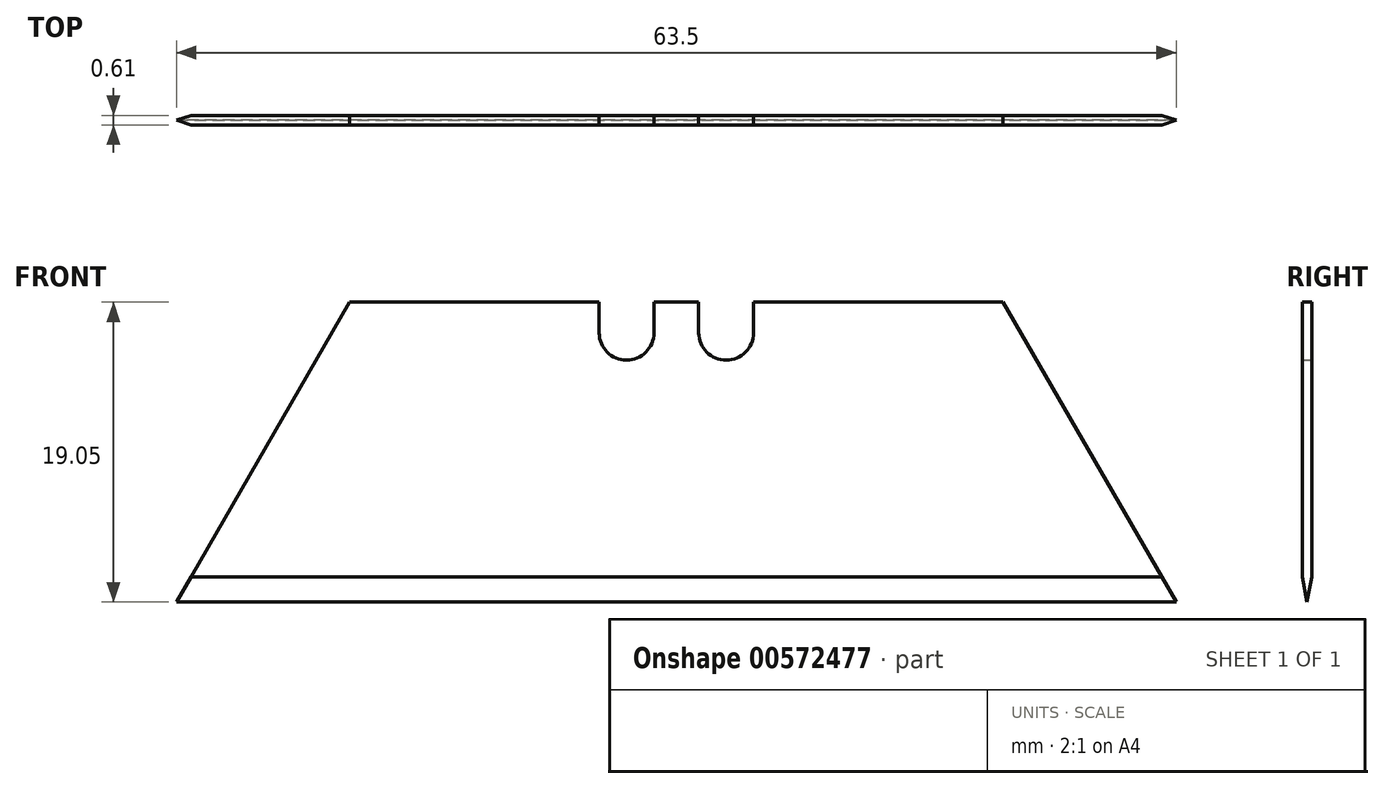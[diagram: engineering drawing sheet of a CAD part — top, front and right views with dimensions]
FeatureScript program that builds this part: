
annotation { "Feature Type Name" : "Feature", "Feature Type Description" : "" }
export const myFeature = defineFeature(function(context is Context, id is Id, definition is map)
    precondition{}
    {
        {
            var Q0;
            Q0=qCreatedBy(makeId("Front.planeOp"),FACE);
            var sketch = newSketch(context, id + "F0", { "sketchPlane" : qUnion([Q0])});
            skLineSegment(sketch, "E0", {"start": v(0, 0) * mm, "end": v(31.75, 0) * mm});
            skLineSegment(sketch, "E1", {"start": v(31.75, 0) * mm, "end": v(20.75, 19.05) * mm});
            skLineSegment(sketch, "E2", {"start": v(20.75, 19.05) * mm, "end": v(0, 19.05) * mm});
            skLineSegment(sketch, "E3", {"start": v(0, 19.05) * mm, "end": v(0, 0) * mm});
            skSolve(sketch);
        }
        {
            var Q0;
            Q0=makeQuery(id+"F0.imprint","IMPRINT",FACE,{"disambiguationData":[TD([[makeQuery(id+"F0.imprint","IMPRINT",EDGE,{"derivedFrom":sQuery(id+"F0.wireOp",EDGE,"E0")}),1.0]])]});
            extrude(context, id + "F1", {"entities" : qUnion([Q0]), "depth" : 0.6 * mm, "offsetDistance" : 25.4 * mm});
        }
        {
            var Q0;
            Q0=qCreatedBy(makeId("Front.planeOp"),FACE);
            var sketch = newSketch(context, id + "F2", { "sketchPlane" : qUnion([Q0])});
            skLineSegment(sketch, "E4.0.0", {"start": v(20.75, 19.05) * mm, "end": v(0, 19.05) * mm});
            skLineSegment(sketch, "E4.0.1", {"start": v(0, 19.05) * mm, "end": v(0, 0) * mm});
            skLineSegment(sketch, "E4.0.2", {"start": v(0, 0) * mm, "end": v(31.75, 0) * mm});
            skLineSegment(sketch, "E4.0.3", {"start": v(31.75, 0) * mm, "end": v(20.75, 19.05) * mm});
            skLineSegment(sketch, "E5.bottom", {"start": v(4.9, 17.1) * mm, "end": v(1.42, 17.1) * mm});
            skLineSegment(sketch, "E5.top", {"start": v(4.9, 21) * mm, "end": v(1.42, 21) * mm});
            skLineSegment(sketch, "E5.left", {"start": v(4.9, 17.1) * mm, "end": v(4.9, 21) * mm});
            skLineSegment(sketch, "E5.right", {"start": v(1.42, 17.1) * mm, "end": v(1.42, 21) * mm});
            skPoint(sketch, "E5.middle", {"position": v(3.16, 19.05) * mm});
            skArc(sketch, "E6", {"start": v(1.42, 17.1) * mm, "mid": v(3.16, 15.37) * mm, "end": v(4.9, 17.1) * mm});
            skSolve(sketch);
        }
        {
            var Q0;
            Q0=makeQuery(id+"F2.imprint","IMPRINT",FACE,{"disambiguationData":[TD([[makeQuery(id+"F2.imprint","IMPRINT",EDGE,{"derivedFrom":sQuery(id+"F2.wireOp",EDGE,"E5.bottom")}),1.0]])]});
            var Q1;
            {var subQ5=sQuery(id+"F2.wireOp",EDGE,"E5.bottom");Q1=makeQuery(id+"F2.imprint","IMPRINT",FACE,{"disambiguationData":[TD([[makeQuery(id+"F2.imprint","IMPRINT",EDGE,{"derivedFrom":subQ5}),-1.0]])]});}
            extrude(context, id + "F3", {"entities" : qUnion([Q0, Q1]), "operationType" : NewBodyOperationType.REMOVE, "depth" : 25.4 * mm, "offsetDistance" : 25.4 * mm});
        }
        {
            var Q0;
            Q0=makeQuery(id+"F1.opExtrude","SWEPT_BODY",BODY,{"disambiguationData":[OSD([sQuery(id+"F0.wireOp",EDGE,"E0"),sQuery(id+"F0.wireOp",EDGE,"E1"),sQuery(id+"F0.wireOp",EDGE,"E2"),sQuery(id+"F0.wireOp",EDGE,"E3")])]});
            var Q1;
            Q1=qCreatedBy(makeId("Right.planeOp"),FACE);
            mirror(context, id + "F4", {"operationType" : NewBodyOperationType.ADD, "entities" : qUnion([Q0]), "mirrorPlane" : qUnion([Q1])});
        }
        {
            var Q0;
            {var subQ0=makeQuery(id+"F1.opExtrude","CAP_EDGE",EDGE,{"disambiguationData":[OSD([sQuery(id+"F0.wireOp",EDGE,"E0")])],"isStart":true});Q0=makeQuery(id+"F4.boolean.opBoolean","MERGE",EDGE,{"derivedFrom":[subQ0,makeQuery(id+"F4.opPattern","COPY",EDGE,{"derivedFrom":subQ0,"instanceName":"1"})]});}
            var Q1;
            {var subQ0=makeQuery(id+"F1.opExtrude","CAP_EDGE",EDGE,{"disambiguationData":[OSD([sQuery(id+"F0.wireOp",EDGE,"E0")])],"isStart":false});Q1=makeQuery(id+"F4.boolean.opBoolean","MERGE",EDGE,{"derivedFrom":[subQ0,makeQuery(id+"F4.opPattern","COPY",EDGE,{"derivedFrom":subQ0,"instanceName":"1"})]});}
            chamfer(context, id + "F5", {"entities" : qUnion([Q0, Q1]), "chamferType" : ChamferType.OFFSET_ANGLE, "width" : 1.59 * mm, "oppositeDirection" : true, "angle" : 10.85 * degree, "tangentPropagation" : true});
        }
    });
